# Revit family: 756-100-020-DN150-600
name_source: partatom
category: Pipe Accessories
units: mm (PartAtom-declared; Revit-internal decimal feet)

## family parameters
Always vertical = Yes
Cut with Voids When Loaded = No
Part Type = Valve - Breaks Into
Round Connector Dimension = Use Diameter
Shared = No
Work Plane-Based = No

## types (17) — shared parameters
Body_wallthickness = 10 mm  [stored 0.0328084 ft]
DN150 = Yes
DN150_PN10/16 = 756-0150-1-1400009
DN200 = Yes
DN200_PN10 = 756-0200-1-0400009
DN200_PN16 = 756-0200-1-1400009
DN250 = Yes
DN250_PN16 = 756-0250-1-1400009
DN300 = Yes
DN300_PN10 = 756-0300-1-0400009
DN300_PN16 = 756-0300-1-1400009
DN350 = Yes
DN350_PN10 = 756-0350-1-0400009
DN350_PN16 = 756-0350-1-1400009
DN400 = Yes
DN400_PN10 = 756-0400-1-0400009
DN400_PN16 = 756-0400-1-1400009
DN450 = Yes
DN450_PN10 = 756-0450-1-0400009
DN450_PN16 = 756-0450-1-1400009
DN500 = Yes
DN500_PN10 = 756-0500-1-0400009
DN500_PN16 = 756-0500-1-1400009
DN600 = Yes
DN600_PN10 = 756-0600-1-0400009
DN600_PN16 = 756-0600-1-1400009
Description_ = AVK_SWING_CHECK_VALVE
RF_Cut_Thickness = 5 mm  [stored 0.0164042 ft]
Rib_depth = 15 mm  [stored 0.0492126 ft]
Search_table = 756-100-020-DN150-600
URL_product_pages = https://www.avkvalves.com

## per-type parameters (varying)
- DN150-PN10/16: Bottom_Depth=225 mm; Bottom_width=120 mm; C_rod=9 mm  [stored 0.0295276 ft]; D=117.5 mm; DN=150 mm; DN250_PN10=756-0250-1-0400009; Disc_1=2 mm  [stored 0.00656168 ft]; Disc_2=2 mm  [stored 0.00656168 ft]; Disc_Dia=133 mm; Disc_width=10 mm  [stored 0.0328084 ft]; Flange_OD=142.5 mm; Flange_Thickness=15 mm  [stored 0.0492126 ft]; Gear_box_Mount_Flange_thickness=15 mm  [stored 0.0492126 ft]; Gear_box_Mount_Flange_width=68 mm  [stored 0.223097 ft]; Gear_box_Mount_width=43 mm  [stored 0.141076 ft]; Gear_box_width=88.4 mm; H1=190.5 mm; H2=201 mm; HW_Connecting_Rib=235 mm; HW_Connecting_Rib_ref=226.75 mm; HW_Ref=71 mm; HW_height=268.5 mm; HW_rod_Dia=15 mm  [stored 0.0492126 ft]; Hand_wheel_rod=36.5 mm  [stored 0.119751 ft]; ID (Radius)=75 mm; L=210 mm; L1=1 mm  [stored 0.00328084 ft]; L2=1 mm  [stored 0.00328084 ft]; Pin_Depth=217.5 mm; Pin_dia=30 mm  [stored 0.0984252 ft]; Pin_width=105 mm; Rf_Dia=105.5 mm; Rib_height=129.55 mm; Rib_height_2=48 mm  [stored 0.15748 ft]; Rib_width=180 mm; Rib_width_2=136 mm; W1=155 mm; W2=263 mm; W3=6 mm  [stored 0.019685 ft]; W4=6 mm  [stored 0.019685 ft]; W5=276 mm; offset=3 mm  [stored 0.00984252 ft]
- DN200-PN10: Bottom_Depth=300.15 mm; Bottom_width=140 mm; C_rod=9 mm  [stored 0.0295276 ft]; D=117.5 mm; DN=200.1 mm; DN250_PN10=756-0250-1-0400009; Disc_1=2 mm  [stored 0.00656168 ft]; Disc_2=2 mm  [stored 0.00656168 ft]; Disc_Dia=180 mm; Disc_width=10 mm  [stored 0.0328084 ft]; Flange_OD=170 mm; Flange_Thickness=15 mm  [stored 0.0492126 ft]; Gear_box_Mount_Flange_thickness=15 mm  [stored 0.0492126 ft]; Gear_box_Mount_Flange_width=68 mm  [stored 0.223097 ft]; Gear_box_Mount_width=43 mm  [stored 0.141076 ft]; Gear_box_width=88.4 mm; H1=216.5 mm; H2=225 mm; HW_Connecting_Rib=235 mm; HW_Connecting_Rib_ref=247.75 mm; HW_Ref=71 mm; HW_height=268.5 mm; HW_rod_Dia=15 mm  [stored 0.0492126 ft]; Hand_wheel_rod=31.5 mm  [stored 0.103346 ft]; ID (Radius)=100.05 mm; L=230 mm; L1=1 mm  [stored 0.00328084 ft]; L2=1 mm  [stored 0.00328084 ft]; Pin_Depth=270.05 mm; Pin_dia=30 mm  [stored 0.0984252 ft]; Pin_width=115 mm; Rf_Dia=133 mm; Rib_height=154.55 mm; Rib_height_2=46.5 mm; Rib_width=200 mm; Rib_width_2=136 mm; W1=182 mm; W2=279 mm; W3=6 mm  [stored 0.019685 ft]; W4=6 mm  [stored 0.019685 ft]; W5=276 mm; offset=5 mm  [stored 0.0164042 ft]
- DN250-PN10: Bottom_Depth=375.15 mm; Bottom_width=170 mm; C_rod=14 mm  [stored 0.0459318 ft]; D=117.5 mm; DN=250.1 mm; DN250_PN10=756-0250-1-0400009; Disc_1=2 mm  [stored 0.00656168 ft]; Disc_2=2 mm  [stored 0.00656168 ft]; Disc_Dia=227 mm; Disc_width=15 mm  [stored 0.0492126 ft]; Flange_OD=202.5 mm; Flange_Thickness=15 mm  [stored 0.0492126 ft]; Gear_box_Mount_Flange_thickness=15 mm  [stored 0.0492126 ft]; Gear_box_Mount_Flange_width=62 mm  [stored 0.203412 ft]; Gear_box_Mount_width=37 mm  [stored 0.121391 ft]; Gear_box_width=80.6 mm; H1=250.5 mm; H2=259 mm; HW_Connecting_Rib=235 mm; HW_Connecting_Rib_ref=281.75 mm; HW_Ref=71 mm; HW_height=268.5 mm; HW_rod_Dia=15 mm  [stored 0.0492126 ft]; Hand_wheel_rod=31.5 mm  [stored 0.103346 ft]; ID (Radius)=125.05 mm; L=250 mm; L1=1 mm  [stored 0.00328084 ft]; L2=1 mm  [stored 0.00328084 ft]; Pin_Depth=327.55 mm; Pin_dia=30 mm  [stored 0.0984252 ft]; Pin_width=125 mm; Rf_Dia=159.5 mm; Rib_height=184.09 mm; Rib_height_2=48 mm  [stored 0.15748 ft]; Rib_width=220 mm; Rib_width_2=124 mm; W1=215 mm; W2=313 mm; W3=6 mm  [stored 0.019685 ft]; W4=6 mm  [stored 0.019685 ft]; W5=276 mm; offset=5 mm  [stored 0.0164042 ft]
- DN300-PN10: Bottom_Depth=450.15 mm; Bottom_width=210 mm; C_rod=14 mm  [stored 0.0459318 ft]; D=115 mm; DN=300.1 mm; DN250_PN10=756-0250-1-0400009; Disc_1=3 mm  [stored 0.00984252 ft]; Disc_2=20 mm  [stored 0.0656168 ft]; Disc_Dia=282.17 mm; Disc_width=15 mm  [stored 0.0492126 ft]; Flange_OD=230 mm; Flange_Thickness=20 mm  [stored 0.0656168 ft]; Gear_box_Mount_Flange_thickness=20 mm  [stored 0.0656168 ft]; Gear_box_Mount_Flange_width=75 mm; Gear_box_Mount_width=45 mm  [stored 0.147638 ft]; Gear_box_width=97.5 mm; H1=281.5 mm; H2=293 mm; HW_Connecting_Rib=230 mm; HW_Connecting_Rib_ref=312.25 mm; HW_Ref=71 mm; HW_height=266 mm; HW_rod_Dia=20 mm  [stored 0.0656168 ft]; Hand_wheel_rod=31 mm  [stored 0.101706 ft]; ID (Radius)=150.05 mm; L=270 mm; L1=1 mm  [stored 0.00328084 ft]; L2=12 mm  [stored 0.0393701 ft]; Pin_Depth=380.05 mm; Pin_dia=40 mm  [stored 0.131234 ft]; Pin_width=135 mm; Rf_Dia=185 mm; Rib_height=209.09 mm; Rib_height_2=51.5 mm  [stored 0.168963 ft]; Rib_width=230 mm; Rib_width_2=150 mm; W1=242 mm; W2=343 mm; W3=6 mm  [stored 0.019685 ft]; W4=104 mm; W5=276 mm; offset=6 mm  [stored 0.019685 ft]
- DN350-PN10: Bottom_Depth=525.15 mm; Bottom_width=210 mm; C_rod=19 mm  [stored 0.062336 ft]; D=115 mm; DN=350.1 mm; DN250_PN10=756-0250-1-0400009; Disc_1=20 mm  [stored 0.0656168 ft]; Disc_2=20 mm  [stored 0.0656168 ft]; Disc_Dia=334.2 mm; Disc_width=20 mm  [stored 0.0656168 ft]; Flange_OD=260 mm; Flange_Thickness=20 mm  [stored 0.0656168 ft]; Gear_box_Mount_Flange_thickness=20 mm  [stored 0.0656168 ft]; Gear_box_Mount_Flange_width=80 mm; Gear_box_Mount_width=50 mm  [stored 0.164042 ft]; Gear_box_width=104 mm; H1=308 mm; H2=318 mm; HW_Connecting_Rib=230 mm; HW_Connecting_Rib_ref=338.5 mm; HW_Ref=71 mm; HW_height=266 mm; HW_rod_Dia=20 mm  [stored 0.0656168 ft]; Hand_wheel_rod=30.5 mm  [stored 0.100066 ft]; ID (Radius)=175.05 mm; L=290 mm; L1=20 mm  [stored 0.0656168 ft]; L2=26 mm; Pin_Depth=435.05 mm; Pin_dia=40 mm  [stored 0.131234 ft]; Pin_width=145 mm; Rf_Dia=214.5 mm; Rib_height=236.36 mm; Rib_height_2=48 mm  [stored 0.15748 ft]; Rib_width=250 mm; Rib_width_2=160 mm; W1=272 mm; W2=369 mm; W3=151 mm; W4=173 mm; W5=276 mm; offset=3 mm  [stored 0.00984252 ft]
- DN400-PN10: Bottom_Depth=600.15 mm; Bottom_width=260 mm; C_rod=24 mm  [stored 0.0787402 ft]; D=190 mm; DN=400.1 mm; DN250_PN10=756-0250-1-0400009; Disc_1=20 mm  [stored 0.0656168 ft]; Disc_2=20 mm  [stored 0.0656168 ft]; Disc_Dia=383 mm; Disc_width=25 mm  [stored 0.082021 ft]; Flange_OD=290 mm; Flange_Thickness=20 mm  [stored 0.0656168 ft]; Gear_box_Mount_Flange_thickness=20 mm  [stored 0.0656168 ft]; Gear_box_Mount_Flange_width=75 mm; Gear_box_Mount_width=45 mm  [stored 0.147638 ft]; Gear_box_width=97.5 mm; H1=339 mm; H2=349 mm; HW_Connecting_Rib=380 mm; HW_Connecting_Rib_ref=371 mm; HW_Ref=80 mm; HW_height=296 mm; HW_rod_Dia=20 mm  [stored 0.0656168 ft]; Hand_wheel_rod=32 mm  [stored 0.104987 ft]; ID (Radius)=200.05 mm; L=310 mm; L1=35 mm  [stored 0.114829 ft]; L2=41 mm  [stored 0.134514 ft]; Pin_Depth=490.05 mm; Pin_dia=40 mm  [stored 0.131234 ft]; Pin_width=155 mm; Rf_Dia=240 mm; Rib_height=263.64 mm; Rib_height_2=49 mm  [stored 0.160761 ft]; Rib_width=270 mm; Rib_width_2=150 mm; W1=302 mm; W2=403 mm; W3=215 mm; W4=232 mm; W5=306 mm; offset=3 mm  [stored 0.00984252 ft]
- DN450-PN10: Bottom_Depth=675.15 mm; Bottom_width=280 mm; C_rod=24 mm  [stored 0.0787402 ft]; D=185 mm; DN=450.1 mm; DN250_PN10=756-0250-1-0400009
756-0250-1-0400009; Disc_1=20 mm  [stored 0.0656168 ft]; Disc_2=20 mm  [stored 0.0656168 ft]; Disc_Dia=430 mm; Disc_width=25 mm  [stored 0.082021 ft]; Flange_OD=320 mm; Flange_Thickness=30 mm  [stored 0.0984252 ft]; Gear_box_Mount_Flange_thickness=30 mm  [stored 0.0984252 ft]; Gear_box_Mount_Flange_width=92.5 mm; Gear_box_Mount_width=58 mm  [stored 0.190289 ft]; Gear_box_width=120.25 mm; H1=360 mm; H2=389 mm; HW_Connecting_Rib=370 mm; HW_Connecting_Rib_ref=400 mm; HW_Ref=86 mm; HW_height=291 mm; HW_rod_Dia=30 mm  [stored 0.0984252 ft]; Hand_wheel_rod=30 mm  [stored 0.0984252 ft]; ID (Radius)=225.05 mm; L=330 mm; L1=48 mm  [stored 0.15748 ft]; L2=55 mm  [stored 0.180446 ft]; Pin_Depth=545.05 mm; Pin_dia=60 mm  [stored 0.19685 ft]; Pin_width=165 mm; Rf_Dia=265 mm; Rib_height=290.91 mm; Rib_height_2=40 mm  [stored 0.131234 ft]; Rib_width=270 mm; Rib_width_2=185 mm; W1=332 mm; W2=440 mm; W3=267 mm; W4=284 mm; W5=306 mm; offset=3 mm  [stored 0.00984252 ft]
- DN500-PN10: Bottom_Depth=750.15 mm; Bottom_width=320 mm; C_rod=34 mm; D=185 mm; DN=500.1 mm; DN250_PN10=756-0250-1-0400009; Disc_1=20 mm  [stored 0.0656168 ft]; Disc_2=20 mm  [stored 0.0656168 ft]; Disc_Dia=480.61 mm; Disc_width=35 mm  [stored 0.114829 ft]; Flange_OD=335 mm; Flange_Thickness=30 mm  [stored 0.0984252 ft]; Gear_box_Mount_Flange_thickness=30 mm  [stored 0.0984252 ft]; Gear_box_Mount_Flange_width=92.5 mm; Gear_box_Mount_width=58 mm  [stored 0.190289 ft]; Gear_box_width=120.25 mm; H1=390 mm; H2=417 mm; HW_Connecting_Rib=370 mm; HW_Connecting_Rib_ref=429 mm; HW_Ref=86 mm; HW_height=291 mm; HW_rod_Dia=30 mm  [stored 0.0984252 ft]; Hand_wheel_rod=30 mm  [stored 0.0984252 ft]; ID (Radius)=250.05 mm; L=350 mm; L1=63 mm  [stored 0.206693 ft]; L2=69 mm; Pin_Depth=585.05 mm; Pin_dia=60 mm  [stored 0.19685 ft]; Pin_width=175 mm; Rf_Dia=291 mm; Rib_height=304.55 mm; Rib_height_2=55 mm  [stored 0.180446 ft]; Rib_width=290 mm; Rib_width_2=185 mm; W1=338 mm; W2=468 mm; W3=322 mm; W4=335 mm; W5=306 mm; offset=3 mm  [stored 0.00984252 ft]
- DN600-PN10: Bottom_Depth=900.15 mm; Bottom_width=400 mm; C_rod=34 mm; D=235 mm; DN=600.1 mm; DN250_PN10=756-0250-1-0400009; Disc_1=20 mm  [stored 0.0656168 ft]; Disc_2=20 mm  [stored 0.0656168 ft]; Disc_Dia=582 mm; Disc_width=35 mm  [stored 0.114829 ft]; Flange_OD=390 mm; Flange_Thickness=30 mm  [stored 0.0984252 ft]; Gear_box_Mount_Flange_thickness=30 mm  [stored 0.0984252 ft]; Gear_box_Mount_Flange_width=102.5 mm; Gear_box_Mount_width=62.5 mm  [stored 0.205052 ft]; Gear_box_width=133.25 mm; H1=465 mm; H2=476 mm; HW_Connecting_Rib=470 mm; HW_Connecting_Rib_ref=500.5 mm; HW_Ref=104 mm; HW_height=401 mm; HW_rod_Dia=30 mm  [stored 0.0984252 ft]; Hand_wheel_rod=31.5 mm  [stored 0.103346 ft]; ID (Radius)=300.05 mm; L=390 mm; L1=94 mm; L2=100 mm; Pin_Depth=690.05 mm; Pin_dia=60 mm  [stored 0.19685 ft]; Pin_width=195 mm; Rf_Dia=341 mm; Rib_height=354.55 mm; Rib_height_2=75 mm; Rib_width=330 mm; Rib_width_2=205 mm; W1=393 mm; W2=536 mm; W3=426 mm; W4=437 mm; W5=416 mm; offset=3 mm  [stored 0.00984252 ft]
- DN200-PN16: Bottom_Depth=300.24 mm; Bottom_width=140 mm; C_rod=9 mm  [stored 0.0295276 ft]; D=117.5 mm; DN=200.16 mm; DN250_PN10=756-0250-1-0400009; Disc_1=2 mm  [stored 0.00656168 ft]; Disc_2=2 mm  [stored 0.00656168 ft]; Disc_Dia=180 mm; Disc_width=10 mm  [stored 0.0328084 ft]; Flange_OD=170 mm; Flange_Thickness=15 mm  [stored 0.0492126 ft]; Gear_box_Mount_Flange_thickness=15 mm  [stored 0.0492126 ft]; Gear_box_Mount_Flange_width=68 mm  [stored 0.223097 ft]; Gear_box_Mount_width=43 mm  [stored 0.141076 ft]; Gear_box_width=88.4 mm; H1=216.5 mm; H2=225 mm; HW_Connecting_Rib=235 mm; HW_Connecting_Rib_ref=247.75 mm; HW_Ref=71 mm; HW_height=268.5 mm; HW_rod_Dia=15 mm  [stored 0.0492126 ft]; Hand_wheel_rod=31.5 mm  [stored 0.103346 ft]; ID (Radius)=100.08 mm; L=230 mm; L1=1 mm  [stored 0.00328084 ft]; L2=1 mm  [stored 0.00328084 ft]; Pin_Depth=270.08 mm; Pin_dia=30 mm  [stored 0.0984252 ft]; Pin_width=115 mm; Rf_Dia=133 mm; Rib_height=154.55 mm; Rib_height_2=46.5 mm; Rib_width=200 mm; Rib_width_2=136 mm; W1=182 mm; W2=279 mm; W3=6 mm  [stored 0.019685 ft]; W4=6 mm  [stored 0.019685 ft]; W5=276 mm; offset=5 mm  [stored 0.0164042 ft]
- DN250-PN16: Bottom_Depth=375.24 mm; Bottom_width=170 mm; C_rod=14 mm  [stored 0.0459318 ft]; D=117.5 mm; DN=250.16 mm; DN250_PN10=756-0250-1-0400009; Disc_1=2 mm  [stored 0.00656168 ft]; Disc_2=2 mm  [stored 0.00656168 ft]; Disc_Dia=227 mm; Disc_width=15 mm  [stored 0.0492126 ft]; Flange_OD=202.5 mm; Flange_Thickness=15 mm  [stored 0.0492126 ft]; Gear_box_Mount_Flange_thickness=15 mm  [stored 0.0492126 ft]; Gear_box_Mount_Flange_width=62 mm  [stored 0.203412 ft]; Gear_box_Mount_width=37 mm  [stored 0.121391 ft]; Gear_box_width=80.6 mm; H1=250.5 mm; H2=259 mm; HW_Connecting_Rib=235 mm; HW_Connecting_Rib_ref=281.75 mm; HW_Ref=71 mm; HW_height=268.5 mm; HW_rod_Dia=15 mm  [stored 0.0492126 ft]; Hand_wheel_rod=31.5 mm  [stored 0.103346 ft]; ID (Radius)=125.08 mm; L=250 mm; L1=1 mm  [stored 0.00328084 ft]; L2=1 mm  [stored 0.00328084 ft]; Pin_Depth=327.58 mm; Pin_dia=30 mm  [stored 0.0984252 ft]; Pin_width=125 mm; Rf_Dia=159.5 mm; Rib_height=184.09 mm; Rib_height_2=48 mm  [stored 0.15748 ft]; Rib_width=220 mm; Rib_width_2=124 mm; W1=215 mm; W2=313 mm; W3=6 mm  [stored 0.019685 ft]; W4=6 mm  [stored 0.019685 ft]; W5=276 mm; offset=5 mm  [stored 0.0164042 ft]
- DN300-PN16: Bottom_Depth=450.24 mm; Bottom_width=210 mm; C_rod=14 mm  [stored 0.0459318 ft]; D=190 mm; DN=300.16 mm; DN250_PN10=756-0250-1-0400009; Disc_1=3 mm  [stored 0.00984252 ft]; Disc_2=20 mm  [stored 0.0656168 ft]; Disc_Dia=282.17 mm; Disc_width=15 mm  [stored 0.0492126 ft]; Flange_OD=230 mm; Flange_Thickness=20 mm  [stored 0.0656168 ft]; Gear_box_Mount_Flange_thickness=20 mm  [stored 0.0656168 ft]; Gear_box_Mount_Flange_width=75 mm; Gear_box_Mount_width=45 mm  [stored 0.147638 ft]; Gear_box_width=97.5 mm; H1=281.5 mm; H2=293 mm; HW_Connecting_Rib=380 mm; HW_Connecting_Rib_ref=312.25 mm; HW_Ref=71 mm; HW_height=296 mm; HW_rod_Dia=20 mm  [stored 0.0656168 ft]; Hand_wheel_rod=31 mm  [stored 0.101706 ft]; ID (Radius)=150.08 mm; L=270 mm; L1=1 mm  [stored 0.00328084 ft]; L2=12 mm  [stored 0.0393701 ft]; Pin_Depth=380.08 mm; Pin_dia=40 mm  [stored 0.131234 ft]; Pin_width=135 mm; Rf_Dia=185 mm; Rib_height=209.09 mm; Rib_height_2=51.5 mm  [stored 0.168963 ft]; Rib_width=230 mm; Rib_width_2=150 mm; W1=242 mm; W2=343 mm; W3=6 mm  [stored 0.019685 ft]; W4=104 mm; W5=306 mm; offset=6 mm  [stored 0.019685 ft]
- DN350-PN16: Bottom_Depth=525.24 mm; Bottom_width=210 mm; C_rod=19 mm  [stored 0.062336 ft]; D=190 mm; DN=350.16 mm; DN250_PN10=756-0250-1-0400009; Disc_1=20 mm  [stored 0.0656168 ft]; Disc_2=20 mm  [stored 0.0656168 ft]; Disc_Dia=334.2 mm; Disc_width=20 mm  [stored 0.0656168 ft]; Flange_OD=260 mm; Flange_Thickness=20 mm  [stored 0.0656168 ft]; Gear_box_Mount_Flange_thickness=20 mm  [stored 0.0656168 ft]; Gear_box_Mount_Flange_width=80 mm; Gear_box_Mount_width=50 mm  [stored 0.164042 ft]; Gear_box_width=104 mm; H1=308 mm; H2=318 mm; HW_Connecting_Rib=380 mm; HW_Connecting_Rib_ref=338.5 mm; HW_Ref=71 mm; HW_height=296 mm; HW_rod_Dia=20 mm  [stored 0.0656168 ft]; Hand_wheel_rod=30.5 mm  [stored 0.100066 ft]; ID (Radius)=175.08 mm; L=290 mm; L1=20 mm  [stored 0.0656168 ft]; L2=26 mm; Pin_Depth=435.08 mm; Pin_dia=40 mm  [stored 0.131234 ft]; Pin_width=145 mm; Rf_Dia=214.5 mm; Rib_height=236.36 mm; Rib_height_2=48 mm  [stored 0.15748 ft]; Rib_width=250 mm; Rib_width_2=160 mm; W1=272 mm; W2=369 mm; W3=151 mm; W4=173 mm; W5=306 mm; offset=3 mm  [stored 0.00984252 ft]
- DN400-PN16: Bottom_Depth=600.24 mm; Bottom_width=260 mm; C_rod=24 mm  [stored 0.0787402 ft]; D=190 mm; DN=400.16 mm; DN250_PN10=756-0250-1-0400009; Disc_1=20 mm  [stored 0.0656168 ft]; Disc_2=20 mm  [stored 0.0656168 ft]; Disc_Dia=383 mm; Disc_width=25 mm  [stored 0.082021 ft]; Flange_OD=290 mm; Flange_Thickness=20 mm  [stored 0.0656168 ft]; Gear_box_Mount_Flange_thickness=20 mm  [stored 0.0656168 ft]; Gear_box_Mount_Flange_width=75 mm; Gear_box_Mount_width=45 mm  [stored 0.147638 ft]; Gear_box_width=97.5 mm; H1=339 mm; H2=349 mm; HW_Connecting_Rib=380 mm; HW_Connecting_Rib_ref=371 mm; HW_Ref=80 mm; HW_height=296 mm; HW_rod_Dia=20 mm  [stored 0.0656168 ft]; Hand_wheel_rod=32 mm  [stored 0.104987 ft]; ID (Radius)=200.08 mm; L=310 mm; L1=35 mm  [stored 0.114829 ft]; L2=41 mm  [stored 0.134514 ft]; Pin_Depth=490.08 mm; Pin_dia=40 mm  [stored 0.131234 ft]; Pin_width=155 mm; Rf_Dia=240 mm; Rib_height=263.64 mm; Rib_height_2=49 mm  [stored 0.160761 ft]; Rib_width=270 mm; Rib_width_2=150 mm; W1=302 mm; W2=403 mm; W3=215 mm; W4=232 mm; W5=306 mm; offset=3 mm  [stored 0.00984252 ft]
- DN450-PN16: Bottom_Depth=675.24 mm; Bottom_width=280 mm; C_rod=24 mm  [stored 0.0787402 ft]; D=235 mm; DN=450.16 mm; DN250_PN10=756-0250-1-0400009; Disc_1=20 mm  [stored 0.0656168 ft]; Disc_2=20 mm  [stored 0.0656168 ft]; Disc_Dia=430 mm; Disc_width=25 mm  [stored 0.082021 ft]; Flange_OD=320 mm; Flange_Thickness=30 mm  [stored 0.0984252 ft]; Gear_box_Mount_Flange_thickness=30 mm  [stored 0.0984252 ft]; Gear_box_Mount_Flange_width=92.5 mm; Gear_box_Mount_width=58 mm  [stored 0.190289 ft]; Gear_box_width=120.25 mm; H1=360 mm; H2=389 mm; HW_Connecting_Rib=470 mm; HW_Connecting_Rib_ref=400 mm; HW_Ref=86 mm; HW_height=401 mm; HW_rod_Dia=30 mm  [stored 0.0984252 ft]; Hand_wheel_rod=30 mm  [stored 0.0984252 ft]; ID (Radius)=225.08 mm; L=330 mm; L1=48 mm  [stored 0.15748 ft]; L2=55 mm  [stored 0.180446 ft]; Pin_Depth=545.08 mm; Pin_dia=60 mm  [stored 0.19685 ft]; Pin_width=165 mm; Rf_Dia=265 mm; Rib_height=290.91 mm; Rib_height_2=40 mm  [stored 0.131234 ft]; Rib_width=270 mm; Rib_width_2=185 mm; W1=332 mm; W2=440 mm; W3=267 mm; W4=284 mm; W5=416 mm; offset=3 mm  [stored 0.00984252 ft]
- DN500-PN16: Bottom_Depth=750.24 mm; Bottom_width=320 mm; C_rod=34 mm; D=235 mm; DN=500.16 mm; DN250_PN10=756-0250-1-0400009; Disc_1=20 mm  [stored 0.0656168 ft]; Disc_2=20 mm  [stored 0.0656168 ft]; Disc_Dia=480.61 mm; Disc_width=35 mm  [stored 0.114829 ft]; Flange_OD=335 mm; Flange_Thickness=30 mm  [stored 0.0984252 ft]; Gear_box_Mount_Flange_thickness=30 mm  [stored 0.0984252 ft]; Gear_box_Mount_Flange_width=92.5 mm; Gear_box_Mount_width=58 mm  [stored 0.190289 ft]; Gear_box_width=120.25 mm; H1=390 mm; H2=426 mm; HW_Connecting_Rib=470 mm; HW_Connecting_Rib_ref=433.5 mm; HW_Ref=86 mm; HW_height=401 mm; HW_rod_Dia=30 mm  [stored 0.0984252 ft]; Hand_wheel_rod=30 mm  [stored 0.0984252 ft]; ID (Radius)=250.08 mm; L=350 mm; L1=63 mm  [stored 0.206693 ft]; L2=69 mm; Pin_Depth=585.08 mm; Pin_dia=60 mm  [stored 0.19685 ft]; Pin_width=175 mm; Rf_Dia=291 mm; Rib_height=304.55 mm; Rib_height_2=55 mm  [stored 0.180446 ft]; Rib_width=290 mm; Rib_width_2=185 mm; W1=371 mm; W2=477 mm; W3=322 mm; W4=335 mm; W5=416 mm; offset=3 mm  [stored 0.00984252 ft]
- DN600-PN16: Bottom_Depth=900.24 mm; Bottom_width=400 mm; C_rod=34 mm; D=285 mm; DN=600.16 mm; DN250_PN10=756-0250-1-0400009; Disc_1=20 mm  [stored 0.0656168 ft]; Disc_2=20 mm  [stored 0.0656168 ft]; Disc_Dia=582 mm; Disc_width=35 mm  [stored 0.114829 ft]; Flange_OD=390 mm; Flange_Thickness=30 mm  [stored 0.0984252 ft]; Gear_box_Mount_Flange_thickness=30 mm  [stored 0.0984252 ft]; Gear_box_Mount_Flange_width=102.5 mm; Gear_box_Mount_width=62.5 mm  [stored 0.205052 ft]; Gear_box_width=133.25 mm; H1=465 mm; H2=502 mm; HW_Connecting_Rib=570 mm; HW_Connecting_Rib_ref=510.5 mm; HW_Ref=104 mm; HW_height=441 mm; HW_rod_Dia=30 mm  [stored 0.0984252 ft]; Hand_wheel_rod=31.5 mm  [stored 0.103346 ft]; ID (Radius)=300.08 mm; L=390 mm; L1=94 mm; L2=100 mm; Pin_Depth=690.08 mm; Pin_dia=60 mm  [stored 0.19685 ft]; Pin_width=195 mm; Rf_Dia=341 mm; Rib_height=354.55 mm; Rib_height_2=75 mm; Rib_width=330 mm; Rib_width_2=205 mm; W1=435 mm; W2=556 mm; W3=426 mm; W4=437 mm; W5=456 mm; offset=3 mm  [stored 0.00984252 ft]

note: [stored X ft] marks values corroborated as IEEE doubles in the binary element streams (Revit-internal decimal feet)

## geometry (parser evidence)
native form markers: Sweep x8
no freeform markers — native parametric forms only
